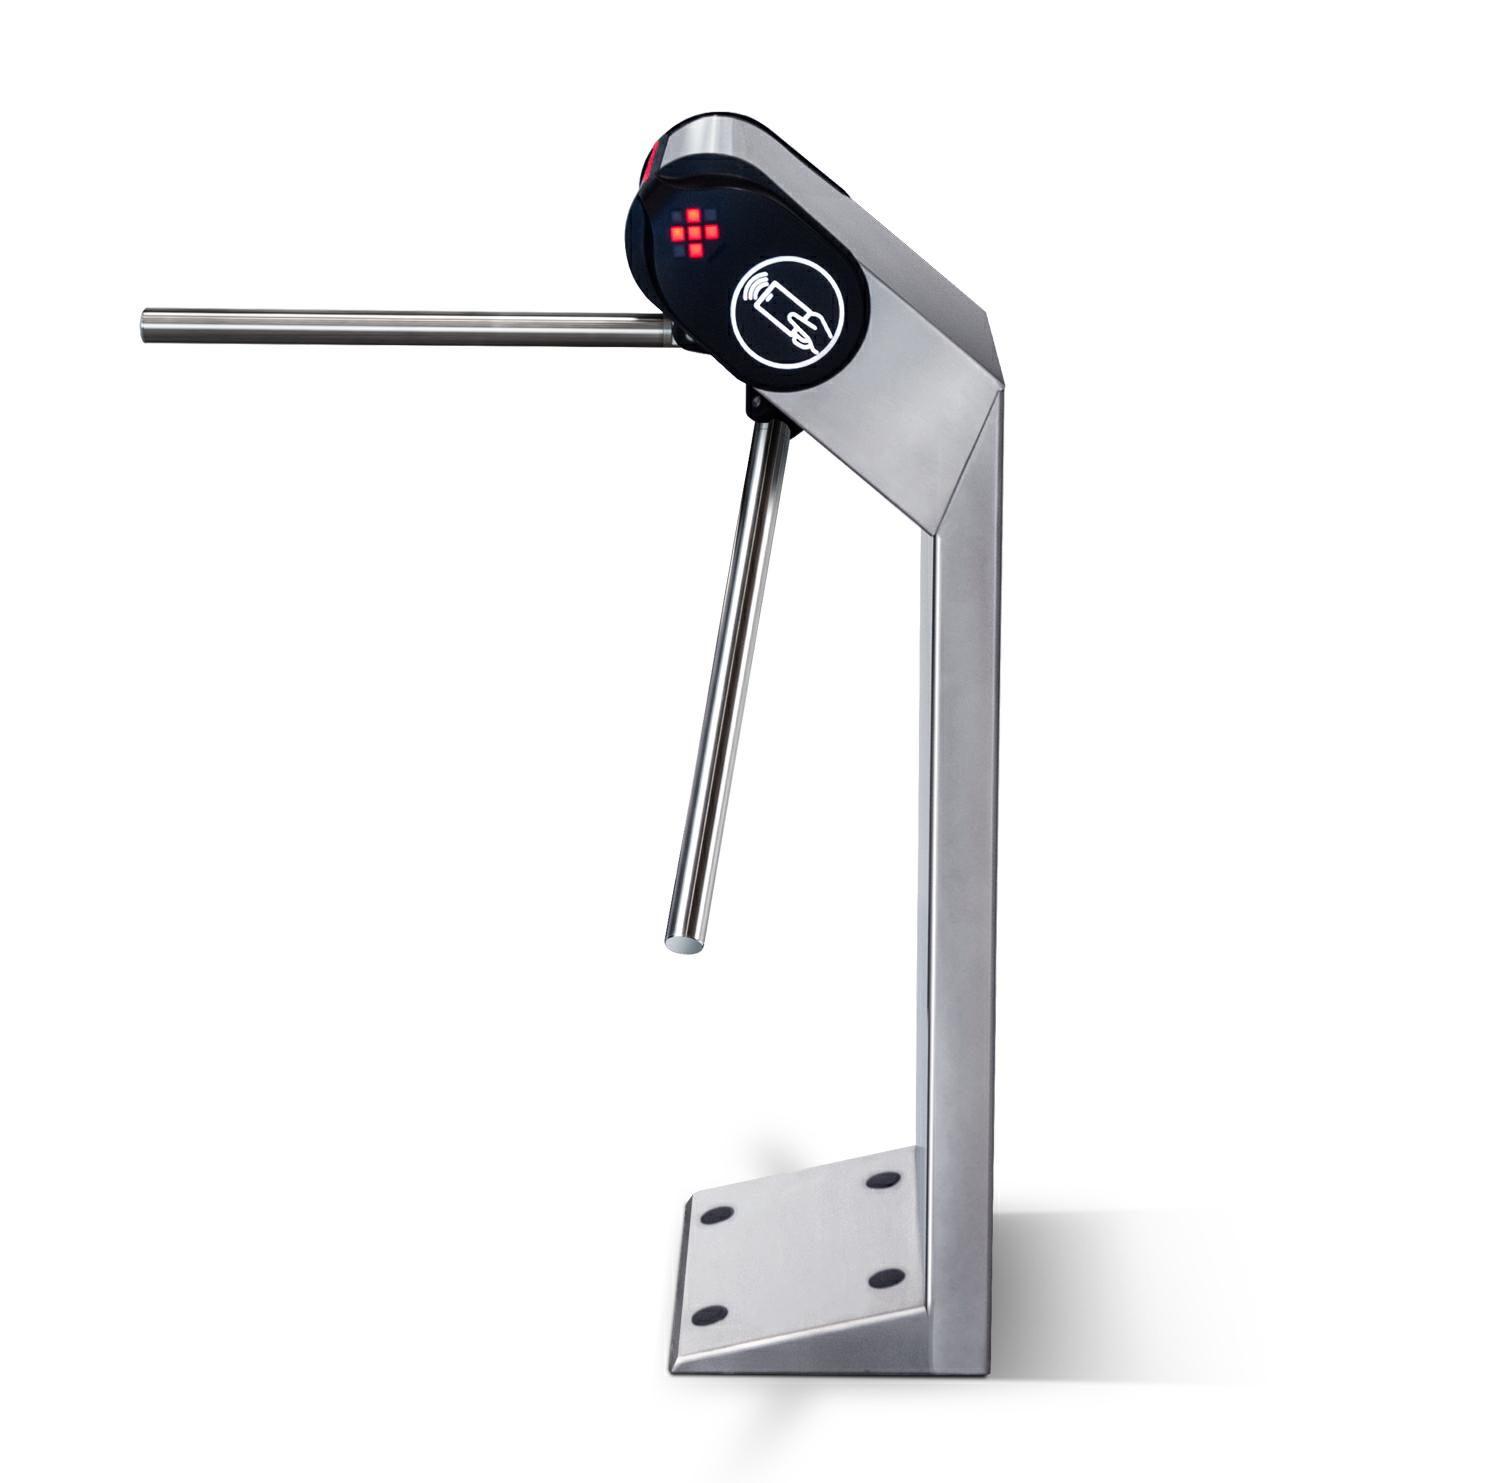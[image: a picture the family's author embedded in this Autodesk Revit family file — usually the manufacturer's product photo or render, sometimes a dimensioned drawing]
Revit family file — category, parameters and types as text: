
# Revit family: Электронная проходная PERCo_KT08.3A
name_source: partatom
category: Оборудование
units: mm (PartAtom-declared; Revit-internal decimal feet)

## family parameters
Всегда вертикально = Да
Классификация = Нет
На основе рабочей плоскости = Нет
Общий = Нет
При загрузке вырезать с полостями = Нет
Размер круглого соединителя = Использовать диаметр
Тип детали = Нормальный
Точка расчета площади = Нет

## types (1)
- КТ08.3А
    ADSK_URL страницы изделия = https://www.perco.ru
    ADSK_Единица измерения = шт.
    ADSK_Завод-изготовитель = PERCo
    ADSK_Количество = 1
    ADSK_Масса_Текст = не более 40 кг
    ADSK_Материал наименование = Корпус турникета выполнен из высококачественной нержавеющей стали со вставками из АБС-пластика, планки из нержавеющей стали
    ADSK_Наименование = Электронная проходная PERCo-KT08.3A с автоматическими преграждающими планками Антипаника
    ADSK_Наименование краткое = Электронная проходная KT08.3A
    ADSK_Напряжение = 12 В
    ADSK_Номинальная мощность = 72 Вт
    ADSK_Ток = 6 А
    Габаритные размеры (длина×ширина×высота) = 798×777×1084 мм
    Длина планки = 538 мм
    Емкость картоприемника = Не предусмотрено
    Изображение типоразмера = <Нет>
    Материал панелей = PERCo_Черный
    Матриал турникета = PERCo_Нержавейка
    Наличие сканеров отпечатка пальцев = Нет
    Наличие сканеров штрих-кода = Нет
    Подключение к электросети = 220 В
    Пропускная способность = 30 чел./мин
    Степень защиты оболочки = IP54
    Стоимость = 0 $
    Температура использования = от –20°С до +55°С
    Тип контроллера = CT03.2
    Тип планки "Антипаника" = Автоматическая
    Формат читаемых карт = EMM, HID Prox
    Цвет планок = PERCo_Сталь, нержавеющая, полированная_планки
    Ширна зоны прохода = 500 мм.
